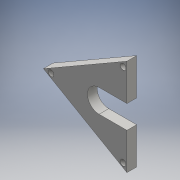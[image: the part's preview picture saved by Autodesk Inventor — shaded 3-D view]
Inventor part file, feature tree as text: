
AUTODESK INVENTOR PART (.ipt)
format: ipt  version: 2016 (Build 200138000, 138)  size: 102,912 bytes
history: native  units: mm
features: extrude x1, sketch x1
ambient origin geometry x8: Origin, YZ Plane, XZ Plane, XY Plane, X Axis, Y Axis, Z Axis, Center Point
bodies: Solid1 (feature_tree)
feature tree (2):
  extrude  "Extrusion1"  Depth=5.0mm
  sketch  "Sketch1"  dims[d0=3.0mm d1=3.0mm d2=43.0mm d4=3.0mm d5=5.0mm d6=0.0mm]
